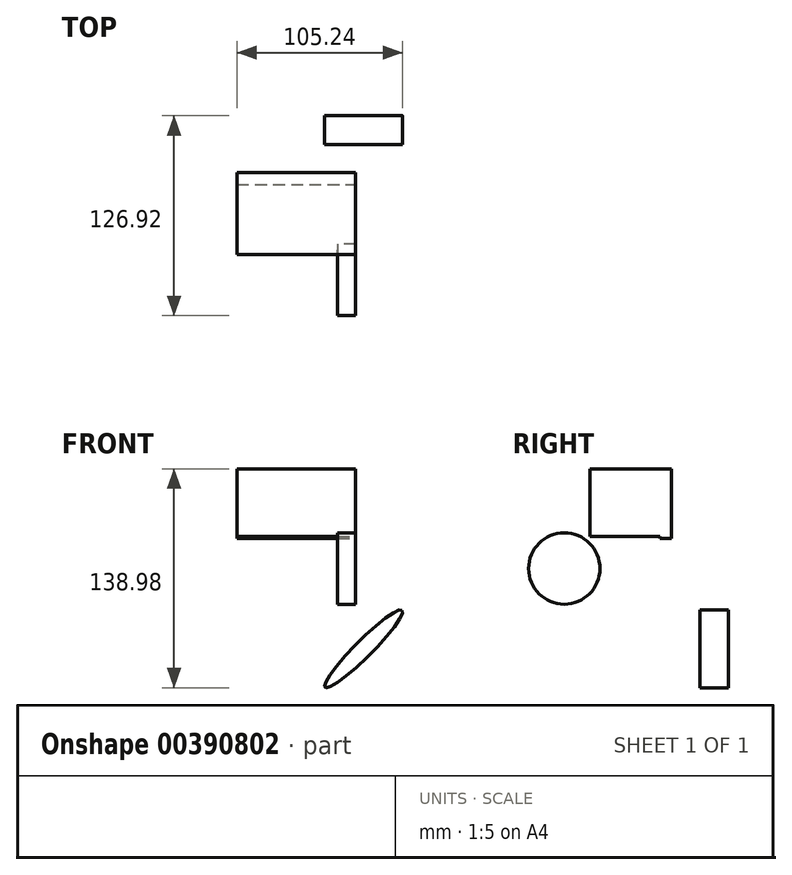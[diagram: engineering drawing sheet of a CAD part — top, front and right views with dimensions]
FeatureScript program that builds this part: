
annotation { "Feature Type Name" : "Feature", "Feature Type Description" : "" }
export const myFeature = defineFeature(function(context is Context, id is Id, definition is map)
    precondition{}
    {
        {
            var Q0;
            Q0=qCreatedBy(makeId("Right.planeOp"),FACE);
            var sketch = newSketch(context, id + "F0", { "sketchPlane" : qUnion([Q0])});
            skCircle(sketch, "E0", {"center": v(-60.67, 82.78) * mm, "radius": 22.64 * mm});
            skSolve(sketch);
        }
        {
            var Q0;
            Q0=makeQuery(id+"F0.imprint","IMPRINT",FACE,{"disambiguationData":[TD([[makeQuery(id+"F0.imprint","IMPRINT",EDGE,{"derivedFrom":sQuery(id+"F0.wireOp",EDGE,"E0")}),1.0]])]});
            extrude(context, id + "F1", {"entities" : qUnion([Q0]), "depth" : 11.54 * mm});
        }
        {
            var Q0;
            Q0=makeQuery(id+"F1.opExtrude","CAP_FACE",FACE,{"disambiguationData":[OSD([sQuery(id+"F0.wireOp",EDGE,"E0")])],"isStart":false});
            var sketch = newSketch(context, id + "F2", { "sketchPlane" : qUnion([Q0])});
            skSolve(sketch);
        }
        {
            var Q0;
            Q0=makeQuery(id+"F2.imprint","IMPRINT",FACE,{"disambiguationData":[TD([[makeQuery(id+"F2.imprint","IMPRINT",EDGE,{"derivedFrom":makeQuery(id+"F1.opExtrude","CAP_EDGE",EDGE,{"disambiguationData":[OSD([sQuery(id+"F0.wireOp",EDGE,"E0")])],"isStart":false})}),1.0]])]});
            var sketch = newSketch(context, id + "F3", { "sketchPlane" : qUnion([Q0])});
            skLineSegment(sketch, "E1.bottom", {"start": v(0, 103.06) * mm, "end": v(-77.6, 103.06) * mm});
            skLineSegment(sketch, "E1.top", {"start": v(0, 74.21) * mm, "end": v(-77.6, 74.21) * mm});
            skLineSegment(sketch, "E1.left", {"start": v(0, 103.06) * mm, "end": v(0, 74.21) * mm});
            skLineSegment(sketch, "E1.right", {"start": v(-77.6, 103.06) * mm, "end": v(-77.6, 74.21) * mm});
            skPoint(sketch, "E1.middle", {"position": v(-38.8, 88.64) * mm});
            skLineSegment(sketch, "E2.bottom", {"start": v(-44.42, 146) * mm, "end": v(23.3, 146) * mm});
            skLineSegment(sketch, "E2.top", {"start": v(-44.42, 83.19) * mm, "end": v(23.3, 83.19) * mm});
            skLineSegment(sketch, "E2.left", {"start": v(-44.42, 146) * mm, "end": v(-44.42, 83.19) * mm});
            skLineSegment(sketch, "E2.right", {"start": v(23.3, 146) * mm, "end": v(23.3, 83.19) * mm});
            skPoint(sketch, "E2.middle", {"position": v(-10.56, 114.6) * mm});
            skLineSegment(sketch, "E3.bottom", {"start": v(7.5, 101.9) * mm, "end": v(-83.81, 101.9) * mm});
            skLineSegment(sketch, "E3.top", {"start": v(7.5, 149.87) * mm, "end": v(-83.81, 149.87) * mm});
            skLineSegment(sketch, "E3.left", {"start": v(7.5, 101.9) * mm, "end": v(7.5, 149.87) * mm});
            skLineSegment(sketch, "E3.right", {"start": v(-83.81, 101.9) * mm, "end": v(-83.81, 149.87) * mm});
            skPoint(sketch, "E3.middle", {"position": v(-38.16, 125.88) * mm});
            skSolve(sketch);
        }
        {
            var Q0;
            {var subQ3=sQuery(id+"F3.wireOp",EDGE,"E1.bottom");var subQ5=sQuery(id+"F3.wireOp",EDGE,"E1.left");var subQ6=makeQuery(id+"F3.imprint","INTERSECT",VERTEX,{"derivedFrom":[subQ3,subQ5]});Q0=makeQuery(id+"F3.imprint","IMPRINT",FACE,{"disambiguationData":[TD([[makeQuery(id+"F3.imprint","IMPRINT",EDGE,{"disambiguationData":[TD([[subQ6,-1.0]])],"derivedFrom":subQ3}),-1.0]])]});}
            extrude(context, id + "F4", {"entities" : qUnion([Q0]), "depth" : -25.4 * mm});
        }
        {
            var Q0;
            Q0=makeQuery(id+"F4.opExtrude","CAP_FACE",FACE,{"disambiguationData":[OSD([sQuery(id+"F3.wireOp",EDGE,"E1.bottom"),sQuery(id+"F3.wireOp",EDGE,"E1.left"),sQuery(id+"F3.wireOp",EDGE,"E2.bottom"),sQuery(id+"F3.wireOp",EDGE,"E2.left"),sQuery(id+"F3.wireOp",EDGE,"E3.bottom"),sQuery(id+"F3.wireOp",EDGE,"E3.left")])],"isStart":false});
            extrude(context, id + "F5", {"entities" : qUnion([Q0]), "operationType" : NewBodyOperationType.ADD, "depth" : 50 * mm});
        }
        {
            var Q0;
            Q0=qCreatedBy(makeId("Front.planeOp"),FACE);
            var sketch = newSketch(context, id + "F6", { "sketchPlane" : qUnion([Q0])});
            skEllipse(sketch, "E4", {"center": v(16.58, 31.82) * mm, "majorRadius": 34.66 * mm, "minorRadius": 5.3 * mm, "majorAxis": v(0.7, 0.7)});
            skSolve(sketch);
        }
        {
            var Q0;
            Q0=makeQuery(id+"F6.imprint","IMPRINT",FACE,{"disambiguationData":[TD([[makeQuery(id+"F6.imprint","IMPRINT",EDGE,{"derivedFrom":sQuery(id+"F6.wireOp",EDGE,"E4")}),1.0]])]});
            extrude(context, id + "F7", {"entities" : qUnion([Q0]), "oppositeDirection" : true, "depth" : 43.6 * mm, "hasSecondDirection" : true, "secondDirectionOppositeDirection" : true, "secondDirectionDepth" : 25.4 * mm});
        }
    });
